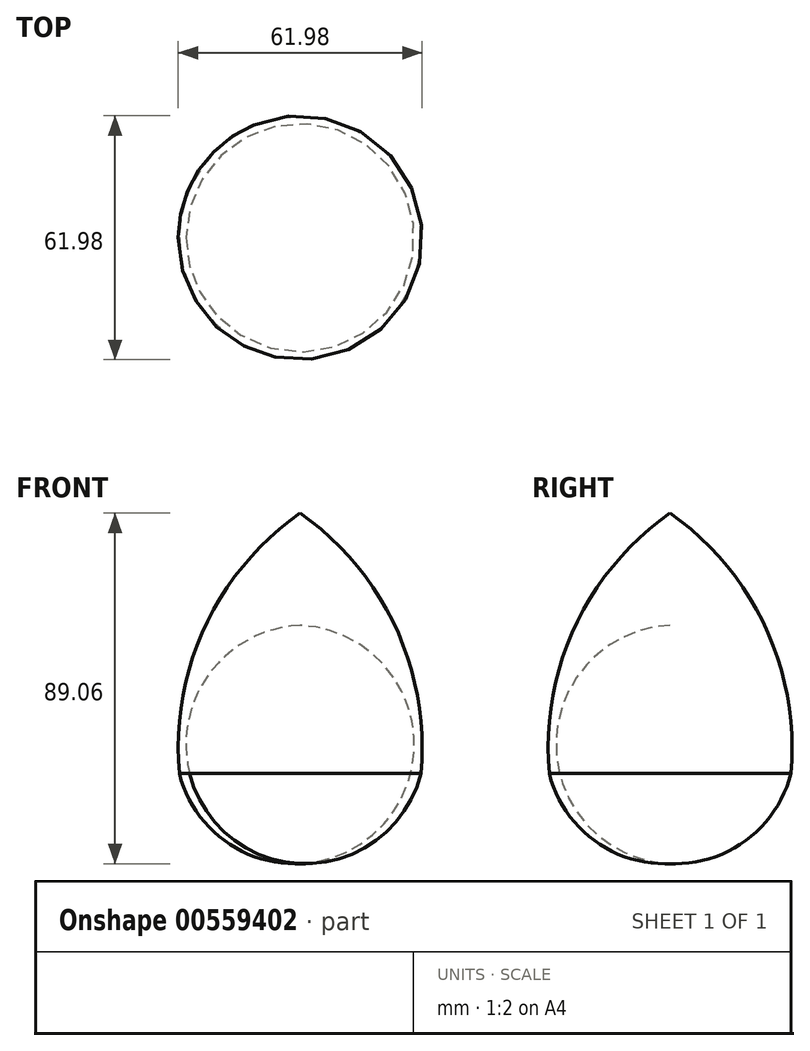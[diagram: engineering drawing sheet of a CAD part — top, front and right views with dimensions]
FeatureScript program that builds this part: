
annotation { "Feature Type Name" : "Feature", "Feature Type Description" : "" }
export const myFeature = defineFeature(function(context is Context, id is Id, definition is map)
    precondition{}
    {
        {
            var Q0;
            Q0=qCreatedBy(makeId("Front.planeOp"),FACE);
            var sketch = newSketch(context, id + "F0", { "sketchPlane" : qUnion([Q0])});
            skArc(sketch, "E0", {"start": v(30.68, 0) * mm, "mid": v(24.25, 37.22) * mm, "end": v(0, 66.17) * mm});
            skArc(sketch, "E1", {"start": v(0, -22.86) * mm, "mid": v(19.4, -16.89) * mm, "end": v(30.68, 0) * mm});
            skLineSegment(sketch, "E2", {"start": v(0, 66.17) * mm, "end": v(0, -22.86) * mm});
            skSolve(sketch);
        }
        {
            var Q0;
            Q0=makeQuery(id+"F0.imprint","IMPRINT",FACE,{"disambiguationData":[TD([[makeQuery(id+"F0.imprint","IMPRINT",EDGE,{"derivedFrom":sQuery(id+"F0.wireOp",EDGE,"E0")}),1.0]])]});
            var Q1;
            Q1=sQuery(id+"F0.wireOp",EDGE,"E2");
            revolve(context, id + "F1", {"entities" : qUnion([Q0]), "axis" : qUnion([Q1]), "revolveType" : RevolveType.FULL});
        }
    });
